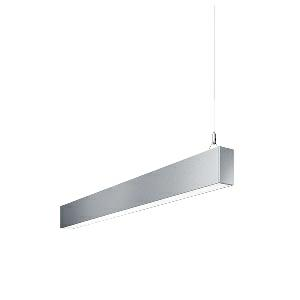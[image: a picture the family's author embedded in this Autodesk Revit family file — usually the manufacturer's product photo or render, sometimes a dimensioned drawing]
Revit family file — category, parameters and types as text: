
# Revit family: dotoo_line_-_dlp_1500_840_d_end_00805824_50c9
name_source: partatom
category: Lighting Fixtures
units: mm (PartAtom-declared; Revit-internal decimal feet)

## family parameters
Cut with Voids When Loaded = No
Host = Face
Light Source = No
Part Type = Normal
Room Calculation Point = No
Round Connector Dimension = Use Diameter
Shared = No

## types (1)
- DOTOO.line - DLP 1500/840/D END (1 x LED, 1350 lm, 4000K)
    Apparent Load = 13 VA
    Approval mark = CE
    CIE Flux Codes = 67 91 98 100 100
    Color Rendering = 80-89
    Color Temperature = 4000K
    Control Gear = Electronic ballast
    Default Elevation = 1800 mm
    Description = DLP 1500/840/D|Suspended luminaire|light source: LED|connected load: 220-240 V, 50/60 Hz|Power consumption: approx. 13 W|standby: approx. 0,20|luminous flux: 1350 lm|luminous efficacy: 103 lm/W|light distribution: Direct|direct ratio: approx. 100 %|colour temperature: Cold white, ca. 4000 K|color rendering index (CRI): >= 80|chromaticity tolerance:  3 SDCM|System of protection: IP 40|technology: Continuously dimmable|luminaire body|material: Sectional aluminium|colour: Silver|lamp cover: Acrylic (PMMA), Clear|mains lead: 1,0 m With free stranded wires|Fastening: Steel cable 0.3 - 0.7 m|glare control: Prism aperture|luminance(L65): <= 3000 cd/m|unified glare rating(4H 8H): <=  19|special features: DALI Load 1x, TouchDIM - dimming via standard switch, Through-wired, up to 18 m on one mains connection, Flicker-free, Suitable as emergency lighting, Mechanical and electrical connection of the individual modules without tools|
    Frequency = 50 Hz
    Height = 110 mm
    Lamp = 1 x LED
    Lamp Light Flux = 1350 lm
    Lamp count = 1
    Length = 1128 mm
    Luminous efficacy = 104 lm/W
    Manufacturer = Waldmann
    ModVariant = No
    Model = 00805824
    Mounting Place = Ceiling
    Mounting Type = Pendant
    Number of Poles = 1
    OnlyDefault = Yes
    Power Factor = 1
    Product Name = DOTOO.line - DLP 1500/840/D END
    Product group = Suspended luminaire
    ProductGroupID = 9
    Protection Class = Protection class I
    Protection Degree = IP 40
    RLX_Detail_Level = 1
    RLX_Emergency_Light_Flux = 0 lm
    RLX_Emergency_Type = 0
    RLX_Emergency_Type_DB = No
    RlxData = <blob elided: 20001 chars, md5=778e6738>
    Socket = socket
    Standby Power = 0 W
    System Light Flux = 1350 lm
    System Power = 13 W
    Type Comments = Product without accessories
    Type Image = 113306000-00692582.jpg
    URL = http://relux.com
    VarID = ---
    Voltage = 230 V
    Voltage Range = 220-240 V
    Weight = 0.00 kg
    Width = 60 mm  [stored 0.19685 ft]

note: [stored X ft] marks values corroborated as IEEE doubles in the binary element streams (Revit-internal decimal feet)

## geometry (parser evidence)
native form markers: Blend x4, Sweep x12
no freeform markers — native parametric forms only
